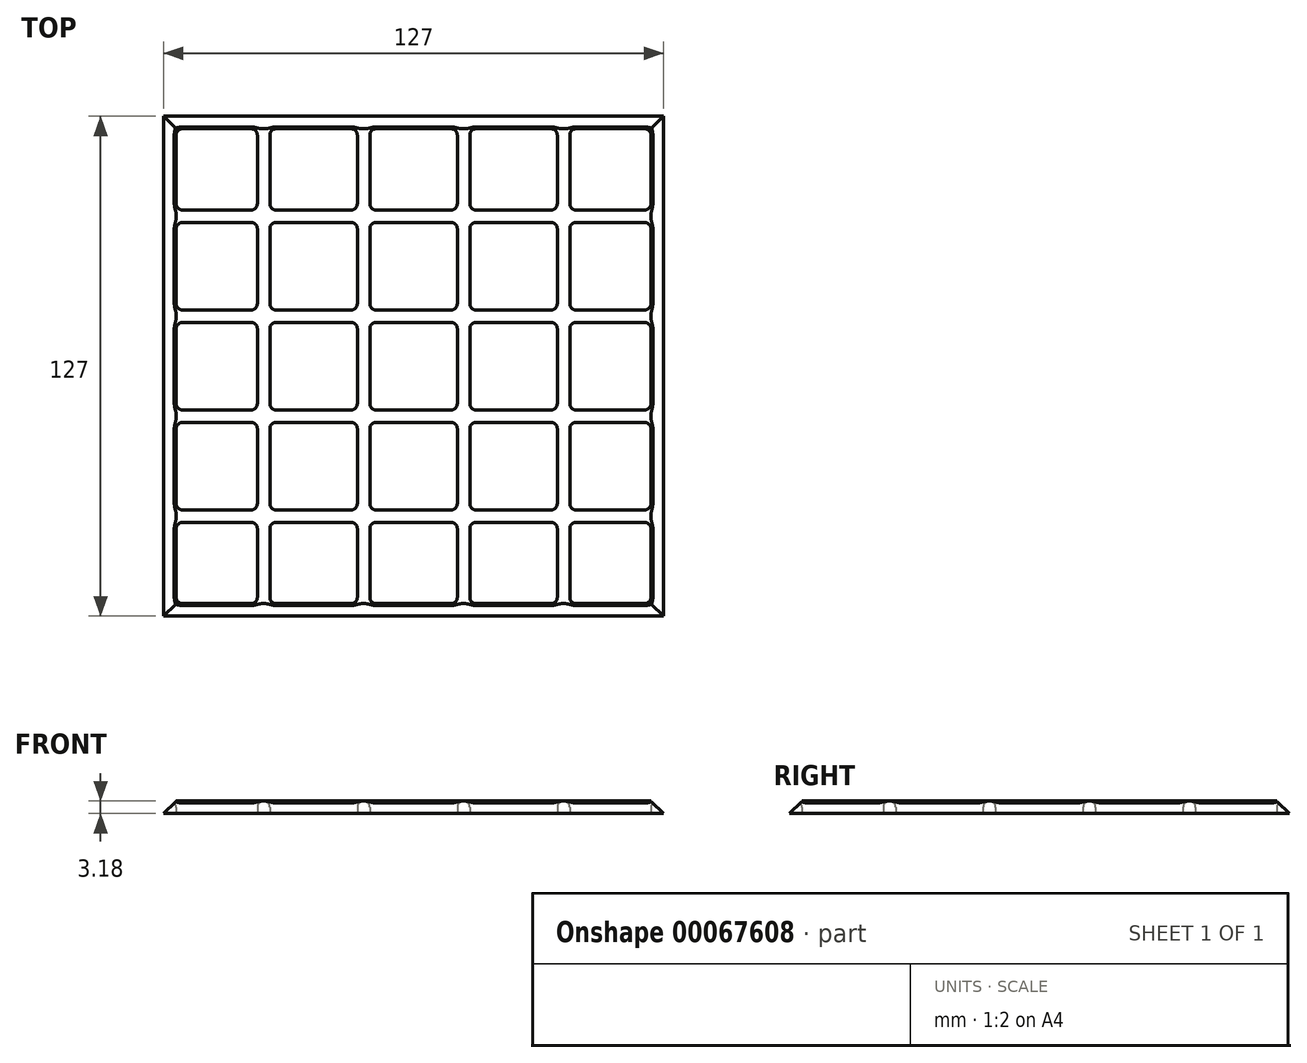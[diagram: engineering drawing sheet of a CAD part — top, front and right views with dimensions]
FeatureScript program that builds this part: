
annotation { "Feature Type Name" : "Feature", "Feature Type Description" : "" }
export const myFeature = defineFeature(function(context is Context, id is Id, definition is map)
    precondition{}
    {
        {
            var Q0;
            Q0=qCreatedBy(makeId("Top.planeOp"),FACE);
            var sketch = newSketch(context, id + "F0", { "sketchPlane" : qUnion([Q0])});
            skLineSegment(sketch, "E0.rect.bottom", {"start": v(-63.5, 63.5) * mm, "end": v(0, 63.5) * mm});
            skLineSegment(sketch, "E0.rect.left", {"start": v(-63.5, 63.5) * mm, "end": v(-63.5, 0) * mm});
            skPoint(sketch, "E0.rect.middle", {"position": v(0, 0) * mm});
            skLineSegment(sketch, "E1.bottom", {"start": v(-58.74, 60.33) * mm, "end": v(-41.27, 60.33) * mm});
            skLineSegment(sketch, "E1.top", {"start": v(-58.74, 39.69) * mm, "end": v(-41.27, 39.69) * mm});
            skLineSegment(sketch, "E1.left", {"start": v(-60.32, 58.74) * mm, "end": v(-60.32, 41.27) * mm});
            skLineSegment(sketch, "E1.right", {"start": v(-39.69, 58.74) * mm, "end": v(-39.69, 41.27) * mm});
            skLineSegment(sketch, "E2.top", {"start": v(-63.5, 38.1) * mm, "end": v(-38.1, 38.1) * mm, "construction": true});
            skLineSegment(sketch, "E2.right", {"start": v(-38.1, 63.5) * mm, "end": v(-38.1, 38.1) * mm, "construction": true});
            skPoint(sketch, "E3.visualSharp", {"position": v(-60.32, 60.33) * mm});
            skArc(sketch, "E3.filletArc", {"start": v(-58.74, 60.33) * mm, "mid": v(-59.86, 59.86) * mm, "end": v(-60.33, 58.74) * mm});
            skPoint(sketch, "E4.visualSharp", {"position": v(-60.33, 39.69) * mm});
            skArc(sketch, "E4.filletArc", {"start": v(-60.32, 41.27) * mm, "mid": v(-59.86, 40.15) * mm, "end": v(-58.74, 39.69) * mm});
            skPoint(sketch, "E5.visualSharp", {"position": v(-39.69, 39.69) * mm});
            skArc(sketch, "E5.filletArc", {"start": v(-41.27, 39.69) * mm, "mid": v(-40.15, 40.15) * mm, "end": v(-39.69, 41.27) * mm});
            skPoint(sketch, "E6.visualSharp", {"position": v(-39.69, 60.33) * mm});
            skArc(sketch, "E6.filletArc", {"start": v(-39.69, 58.74) * mm, "mid": v(-40.15, 59.86) * mm, "end": v(-41.27, 60.33) * mm});
            skPoint(sketch, "E7.oppositeSnap0", {"position": v(-50, 39.69) * mm});
            skLineSegment(sketch, "E7.bottom", {"start": v(-34.92, 60.33) * mm, "end": v(-15.87, 60.33) * mm});
            skLineSegment(sketch, "E7.top", {"start": v(-34.92, 39.69) * mm, "end": v(-15.87, 39.69) * mm});
            skLineSegment(sketch, "E7.left", {"start": v(-36.51, 58.74) * mm, "end": v(-36.51, 41.27) * mm});
            skLineSegment(sketch, "E7.right", {"start": v(-14.29, 58.74) * mm, "end": v(-14.29, 41.27) * mm});
            skLineSegment(sketch, "E8.bottom", {"start": v(-9.53, 60.33) * mm, "end": v(0, 60.33) * mm});
            skLineSegment(sketch, "E8.top", {"start": v(-9.53, 39.69) * mm, "end": v(0, 39.69) * mm});
            skLineSegment(sketch, "E8.left", {"start": v(-11.11, 58.74) * mm, "end": v(-11.11, 41.27) * mm});
            skLineSegment(sketch, "E9", {"start": v(-12.7, 63.5) * mm, "end": v(-12.7, 38.1) * mm, "construction": true});
            skPoint(sketch, "E10.visualSharp", {"position": v(-36.51, 60.33) * mm});
            skArc(sketch, "E10.filletArc", {"start": v(-34.92, 60.33) * mm, "mid": v(-36.05, 59.86) * mm, "end": v(-36.51, 58.74) * mm});
            skPoint(sketch, "E11.visualSharp", {"position": v(-36.51, 39.69) * mm});
            skArc(sketch, "E11.filletArc", {"start": v(-36.51, 41.27) * mm, "mid": v(-36.05, 40.15) * mm, "end": v(-34.92, 39.69) * mm});
            skPoint(sketch, "E12.visualSharp", {"position": v(-14.29, 39.69) * mm});
            skArc(sketch, "E12.filletArc", {"start": v(-15.87, 39.69) * mm, "mid": v(-14.75, 40.15) * mm, "end": v(-14.29, 41.27) * mm});
            skPoint(sketch, "E13.visualSharp", {"position": v(-14.29, 60.33) * mm});
            skArc(sketch, "E13.filletArc", {"start": v(-14.29, 58.74) * mm, "mid": v(-14.75, 59.86) * mm, "end": v(-15.87, 60.33) * mm});
            skPoint(sketch, "E14.visualSharp", {"position": v(-11.11, 60.33) * mm});
            skArc(sketch, "E14.filletArc", {"start": v(-9.53, 60.33) * mm, "mid": v(-10.65, 59.86) * mm, "end": v(-11.11, 58.74) * mm});
            skPoint(sketch, "E15.visualSharp", {"position": v(-11.11, 39.69) * mm});
            skArc(sketch, "E15.filletArc", {"start": v(-11.11, 41.27) * mm, "mid": v(-10.65, 40.15) * mm, "end": v(-9.53, 39.69) * mm});
            skLineSegment(sketch, "E16", {"start": v(-11.11, 0) * mm, "end": v(-14.29, 0) * mm});
            skLineSegment(sketch, "E17", {"start": v(0, 11.11) * mm, "end": v(0, 14.29) * mm});
            skLineSegment(sketch, "E18", {"start": v(0, 60.33) * mm, "end": v(0, 63.5) * mm});
            skLineSegment(sketch, "E19.bottom", {"start": v(-58.74, 36.51) * mm, "end": v(-41.27, 36.51) * mm});
            skLineSegment(sketch, "E19.top", {"start": v(-58.74, 14.29) * mm, "end": v(-41.27, 14.29) * mm});
            skLineSegment(sketch, "E19.left", {"start": v(-60.33, 34.93) * mm, "end": v(-60.33, 15.87) * mm});
            skLineSegment(sketch, "E19.right", {"start": v(-39.69, 34.93) * mm, "end": v(-39.69, 15.87) * mm});
            skLineSegment(sketch, "E20.bottom", {"start": v(-34.93, 36.51) * mm, "end": v(-15.87, 36.51) * mm});
            skLineSegment(sketch, "E20.top", {"start": v(-34.93, 14.29) * mm, "end": v(-15.87, 14.29) * mm});
            skLineSegment(sketch, "E20.left", {"start": v(-36.51, 34.93) * mm, "end": v(-36.51, 15.87) * mm});
            skLineSegment(sketch, "E20.right", {"start": v(-14.29, 34.93) * mm, "end": v(-14.29, 15.87) * mm});
            skLineSegment(sketch, "E21.bottom", {"start": v(-58.74, 11.11) * mm, "end": v(-41.27, 11.11) * mm});
            skLineSegment(sketch, "E21.left", {"start": v(-60.33, 9.52) * mm, "end": v(-60.33, 0) * mm});
            skLineSegment(sketch, "E21.right", {"start": v(-39.69, 9.52) * mm, "end": v(-39.69, 0) * mm});
            skLineSegment(sketch, "E22.bottom", {"start": v(-34.92, 11.11) * mm, "end": v(-15.87, 11.11) * mm});
            skLineSegment(sketch, "E22.left", {"start": v(-36.51, 9.52) * mm, "end": v(-36.51, 0) * mm});
            skLineSegment(sketch, "E22.right", {"start": v(-14.29, 9.53) * mm, "end": v(-14.29, 0) * mm});
            skLineSegment(sketch, "E23.bottom", {"start": v(-9.52, 11.11) * mm, "end": v(0, 11.11) * mm});
            skLineSegment(sketch, "E23.left", {"start": v(-11.11, 9.53) * mm, "end": v(-11.11, 0) * mm});
            skLineSegment(sketch, "E24.bottom", {"start": v(-9.52, 36.51) * mm, "end": v(0, 36.51) * mm});
            skLineSegment(sketch, "E24.top", {"start": v(-9.52, 14.29) * mm, "end": v(0, 14.29) * mm});
            skLineSegment(sketch, "E24.left", {"start": v(-11.11, 34.93) * mm, "end": v(-11.11, 15.87) * mm});
            skLineSegment(sketch, "E25.trimOffspring", {"start": v(-60.33, 0) * mm, "end": v(-63.5, 0) * mm});
            skLineSegment(sketch, "E26.trimOffspring", {"start": v(-36.51, 0) * mm, "end": v(-39.69, 0) * mm});
            skLineSegment(sketch, "E27.trimOffspring", {"start": v(0, 36.51) * mm, "end": v(0, 39.69) * mm});
            skLineSegment(sketch, "E28", {"start": v(-63.5, 12.7) * mm, "end": v(0, 12.7) * mm, "construction": true});
            skPoint(sketch, "E29.visualSharp", {"position": v(-60.33, 36.51) * mm});
            skArc(sketch, "E29.filletArc", {"start": v(-58.74, 36.51) * mm, "mid": v(-59.86, 36.05) * mm, "end": v(-60.33, 34.93) * mm});
            skPoint(sketch, "E30.visualSharp", {"position": v(-60.33, 14.29) * mm});
            skArc(sketch, "E30.filletArc", {"start": v(-60.33, 15.87) * mm, "mid": v(-59.86, 14.75) * mm, "end": v(-58.74, 14.29) * mm});
            skPoint(sketch, "E31.visualSharp", {"position": v(-39.69, 36.51) * mm});
            skArc(sketch, "E31.filletArc", {"start": v(-39.69, 34.93) * mm, "mid": v(-40.15, 36.05) * mm, "end": v(-41.27, 36.51) * mm});
            skPoint(sketch, "E32.visualSharp", {"position": v(-39.69, 14.29) * mm});
            skArc(sketch, "E32.filletArc", {"start": v(-41.27, 14.29) * mm, "mid": v(-40.15, 14.75) * mm, "end": v(-39.69, 15.87) * mm});
            skPoint(sketch, "E33.visualSharp", {"position": v(-36.51, 14.29) * mm});
            skArc(sketch, "E33.filletArc", {"start": v(-36.51, 15.87) * mm, "mid": v(-36.05, 14.75) * mm, "end": v(-34.93, 14.29) * mm});
            skPoint(sketch, "E34.visualSharp", {"position": v(-36.51, 36.51) * mm});
            skArc(sketch, "E34.filletArc", {"start": v(-34.93, 36.51) * mm, "mid": v(-36.05, 36.05) * mm, "end": v(-36.51, 34.93) * mm});
            skPoint(sketch, "E35.visualSharp", {"position": v(-14.29, 36.51) * mm});
            skArc(sketch, "E35.filletArc", {"start": v(-14.29, 34.93) * mm, "mid": v(-14.75, 36.05) * mm, "end": v(-15.87, 36.51) * mm});
            skPoint(sketch, "E36.visualSharp", {"position": v(-14.29, 14.29) * mm});
            skArc(sketch, "E36.filletArc", {"start": v(-15.87, 14.29) * mm, "mid": v(-14.75, 14.75) * mm, "end": v(-14.29, 15.87) * mm});
            skPoint(sketch, "E37.visualSharp", {"position": v(-11.11, 14.29) * mm});
            skArc(sketch, "E37.filletArc", {"start": v(-11.11, 15.87) * mm, "mid": v(-10.65, 14.75) * mm, "end": v(-9.52, 14.29) * mm});
            skPoint(sketch, "E38.visualSharp", {"position": v(-11.11, 36.51) * mm});
            skArc(sketch, "E38.filletArc", {"start": v(-9.52, 36.51) * mm, "mid": v(-10.65, 36.05) * mm, "end": v(-11.11, 34.93) * mm});
            skPoint(sketch, "E39.visualSharp", {"position": v(-11.11, 11.11) * mm});
            skArc(sketch, "E39.filletArc", {"start": v(-9.52, 11.11) * mm, "mid": v(-10.65, 10.65) * mm, "end": v(-11.11, 9.53) * mm});
            skPoint(sketch, "E40.visualSharp", {"position": v(-14.29, 11.11) * mm});
            skArc(sketch, "E40.filletArc", {"start": v(-14.29, 9.53) * mm, "mid": v(-14.75, 10.65) * mm, "end": v(-15.87, 11.11) * mm});
            skPoint(sketch, "E41.visualSharp", {"position": v(-36.51, 11.11) * mm});
            skArc(sketch, "E41.filletArc", {"start": v(-34.92, 11.11) * mm, "mid": v(-36.05, 10.65) * mm, "end": v(-36.51, 9.52) * mm});
            skPoint(sketch, "E42.visualSharp", {"position": v(-60.33, 11.11) * mm});
            skArc(sketch, "E42.filletArc", {"start": v(-58.74, 11.11) * mm, "mid": v(-59.86, 10.65) * mm, "end": v(-60.33, 9.52) * mm});
            skPoint(sketch, "E43.visualSharp", {"position": v(-39.69, 11.11) * mm});
            skArc(sketch, "E43.filletArc", {"start": v(-39.69, 9.52) * mm, "mid": v(-40.15, 10.65) * mm, "end": v(-41.27, 11.11) * mm});
            skSolve(sketch);
        }
        {
            var Q0;
            Q0 = qSketchRegion(id + "F0", true);
            extrude(context, id + "F1", {"entities" : qUnion([Q0]), "depth" : 3.17 * mm});
        }
        {
            var Q0;
            Q0=makeQuery(id+"F1.opExtrude","CAP_EDGE",EDGE,{"disambiguationData":[OSD([sQuery(id+"F0.wireOp",EDGE,"E1.left")])],"isStart":false});
            var Q1;
            Q1=makeQuery(id+"F1.opExtrude","CAP_EDGE",EDGE,{"disambiguationData":[OSD([sQuery(id+"F0.wireOp",EDGE,"E19.left")])],"isStart":false});
            var Q2;
            Q2=makeQuery(id+"F1.opExtrude","CAP_EDGE",EDGE,{"disambiguationData":[OSD([sQuery(id+"F0.wireOp",EDGE,"E20.left")])],"isStart":false});
            var Q3;
            Q3=makeQuery(id+"F1.opExtrude","CAP_EDGE",EDGE,{"disambiguationData":[OSD([sQuery(id+"F0.wireOp",EDGE,"E7.left")])],"isStart":false});
            var Q4;
            Q4=makeQuery(id+"F1.opExtrude","CAP_EDGE",EDGE,{"disambiguationData":[OSD([sQuery(id+"F0.wireOp",EDGE,"E8.left")])],"isStart":false});
            var Q5;
            Q5=makeQuery(id+"F1.opExtrude","CAP_EDGE",EDGE,{"disambiguationData":[OSD([sQuery(id+"F0.wireOp",EDGE,"E24.left")])],"isStart":false});
            var Q6;
            Q6=makeQuery(id+"F1.opExtrude","CAP_EDGE",EDGE,{"disambiguationData":[OSD([sQuery(id+"F0.wireOp",EDGE,"E22.bottom")])],"isStart":false});
            var Q7;
            Q7=makeQuery(id+"F1.opExtrude","CAP_EDGE",EDGE,{"disambiguationData":[OSD([sQuery(id+"F0.wireOp",EDGE,"E21.bottom")])],"isStart":false});
            var Q8;
            Q8=makeQuery(id+"F1.opExtrude","CAP_EDGE",EDGE,{"disambiguationData":[OSD([sQuery(id+"F0.wireOp",EDGE,"E23.bottom")])],"isStart":false});
            fillet(context, id + "F2", {"entities" : qUnion([Q0, Q1, Q2, Q3, Q4, Q5, Q6, Q7, Q8]), "radius" : 1.59 * mm, "tangentPropagation" : true, "allowEdgeOverflow" : false});
        }
        {
            var Q0;
            Q0=makeQuery(id+"F1.opExtrude","SWEPT_BODY",BODY,{"disambiguationData":[OSD([sQuery(id+"F0.wireOp",EDGE,"E0.rect.bottom"),sQuery(id+"F0.wireOp",EDGE,"E0.rect.left"),sQuery(id+"F0.wireOp",EDGE,"E1.bottom"),sQuery(id+"F0.wireOp",EDGE,"E1.top"),sQuery(id+"F0.wireOp",EDGE,"E1.left"),sQuery(id+"F0.wireOp",EDGE,"E1.right"),sQuery(id+"F0.wireOp",EDGE,"E3.filletArc"),sQuery(id+"F0.wireOp",EDGE,"E4.filletArc"),sQuery(id+"F0.wireOp",EDGE,"E5.filletArc"),sQuery(id+"F0.wireOp",EDGE,"E6.filletArc"),sQuery(id+"F0.wireOp",EDGE,"28f6a927-1c7f-40b6-a826-a70ca0bd145b.filletArc"),sQuery(id+"F0.wireOp",EDGE,"E7.bottom"),sQuery(id+"F0.wireOp",EDGE,"E7.top"),sQuery(id+"F0.wireOp",EDGE,"E7.left"),sQuery(id+"F0.wireOp",EDGE,"E7.right"),sQuery(id+"F0.wireOp",EDGE,"E8.bottom"),sQuery(id+"F0.wireOp",EDGE,"E8.top"),sQuery(id+"F0.wireOp",EDGE,"E8.left"),sQuery(id+"F0.wireOp",EDGE,"E10.filletArc"),sQuery(id+"F0.wireOp",EDGE,"E11.filletArc"),sQuery(id+"F0.wireOp",EDGE,"E12.filletArc"),sQuery(id+"F0.wireOp",EDGE,"E13.filletArc"),sQuery(id+"F0.wireOp",EDGE,"E14.filletArc"),sQuery(id+"F0.wireOp",EDGE,"E15.filletArc"),sQuery(id+"F0.wireOp",EDGE,"E16"),sQuery(id+"F0.wireOp",EDGE,"E17"),sQuery(id+"F0.wireOp",EDGE,"E18"),sQuery(id+"F0.wireOp",EDGE,"E19.bottom"),sQuery(id+"F0.wireOp",EDGE,"E19.top"),sQuery(id+"F0.wireOp",EDGE,"E19.left"),sQuery(id+"F0.wireOp",EDGE,"E19.right"),sQuery(id+"F0.wireOp",EDGE,"E20.bottom"),sQuery(id+"F0.wireOp",EDGE,"E20.top"),sQuery(id+"F0.wireOp",EDGE,"E20.left"),sQuery(id+"F0.wireOp",EDGE,"E20.right"),sQuery(id+"F0.wireOp",EDGE,"E21.bottom"),sQuery(id+"F0.wireOp",EDGE,"E21.left"),sQuery(id+"F0.wireOp",EDGE,"E21.right"),sQuery(id+"F0.wireOp",EDGE,"E22.bottom"),sQuery(id+"F0.wireOp",EDGE,"E22.left"),sQuery(id+"F0.wireOp",EDGE,"E22.right"),sQuery(id+"F0.wireOp",EDGE,"E23.bottom"),sQuery(id+"F0.wireOp",EDGE,"E23.left"),sQuery(id+"F0.wireOp",EDGE,"E24.bottom"),sQuery(id+"F0.wireOp",EDGE,"E24.top"),sQuery(id+"F0.wireOp",EDGE,"E24.left"),sQuery(id+"F0.wireOp",EDGE,"E25.trimOffspring"),sQuery(id+"F0.wireOp",EDGE,"E26.trimOffspring"),sQuery(id+"F0.wireOp",EDGE,"E27.trimOffspring")])]});
            var Q1;
            Q1=qCreatedBy(makeId("Right.planeOp"),FACE);
            mirror(context, id + "F3", {"operationType" : NewBodyOperationType.ADD, "entities" : qUnion([Q0]), "mirrorPlane" : qUnion([Q1])});
        }
        {
            var Q0;
            Q0=makeQuery(id+"F1.opExtrude","SWEPT_BODY",BODY,{"disambiguationData":[OSD([sQuery(id+"F0.wireOp",EDGE,"E0.rect.bottom"),sQuery(id+"F0.wireOp",EDGE,"E0.rect.left"),sQuery(id+"F0.wireOp",EDGE,"E1.bottom"),sQuery(id+"F0.wireOp",EDGE,"E1.top"),sQuery(id+"F0.wireOp",EDGE,"E1.left"),sQuery(id+"F0.wireOp",EDGE,"E1.right"),sQuery(id+"F0.wireOp",EDGE,"E3.filletArc"),sQuery(id+"F0.wireOp",EDGE,"E4.filletArc"),sQuery(id+"F0.wireOp",EDGE,"E5.filletArc"),sQuery(id+"F0.wireOp",EDGE,"E6.filletArc"),sQuery(id+"F0.wireOp",EDGE,"28f6a927-1c7f-40b6-a826-a70ca0bd145b.filletArc"),sQuery(id+"F0.wireOp",EDGE,"E7.bottom"),sQuery(id+"F0.wireOp",EDGE,"E7.top"),sQuery(id+"F0.wireOp",EDGE,"E7.left"),sQuery(id+"F0.wireOp",EDGE,"E7.right"),sQuery(id+"F0.wireOp",EDGE,"E8.bottom"),sQuery(id+"F0.wireOp",EDGE,"E8.top"),sQuery(id+"F0.wireOp",EDGE,"E8.left"),sQuery(id+"F0.wireOp",EDGE,"E10.filletArc"),sQuery(id+"F0.wireOp",EDGE,"E11.filletArc"),sQuery(id+"F0.wireOp",EDGE,"E12.filletArc"),sQuery(id+"F0.wireOp",EDGE,"E13.filletArc"),sQuery(id+"F0.wireOp",EDGE,"E14.filletArc"),sQuery(id+"F0.wireOp",EDGE,"E15.filletArc"),sQuery(id+"F0.wireOp",EDGE,"E16"),sQuery(id+"F0.wireOp",EDGE,"E17"),sQuery(id+"F0.wireOp",EDGE,"E18"),sQuery(id+"F0.wireOp",EDGE,"E19.bottom"),sQuery(id+"F0.wireOp",EDGE,"E19.top"),sQuery(id+"F0.wireOp",EDGE,"E19.left"),sQuery(id+"F0.wireOp",EDGE,"E19.right"),sQuery(id+"F0.wireOp",EDGE,"E20.bottom"),sQuery(id+"F0.wireOp",EDGE,"E20.top"),sQuery(id+"F0.wireOp",EDGE,"E20.left"),sQuery(id+"F0.wireOp",EDGE,"E20.right"),sQuery(id+"F0.wireOp",EDGE,"E21.bottom"),sQuery(id+"F0.wireOp",EDGE,"E21.left"),sQuery(id+"F0.wireOp",EDGE,"E21.right"),sQuery(id+"F0.wireOp",EDGE,"E22.bottom"),sQuery(id+"F0.wireOp",EDGE,"E22.left"),sQuery(id+"F0.wireOp",EDGE,"E22.right"),sQuery(id+"F0.wireOp",EDGE,"E23.bottom"),sQuery(id+"F0.wireOp",EDGE,"E23.left"),sQuery(id+"F0.wireOp",EDGE,"E24.bottom"),sQuery(id+"F0.wireOp",EDGE,"E24.top"),sQuery(id+"F0.wireOp",EDGE,"E24.left"),sQuery(id+"F0.wireOp",EDGE,"E25.trimOffspring"),sQuery(id+"F0.wireOp",EDGE,"E26.trimOffspring"),sQuery(id+"F0.wireOp",EDGE,"E27.trimOffspring")])]});
            var Q1;
            Q1=qCreatedBy(makeId("Front.planeOp"),FACE);
            mirror(context, id + "F4", {"operationType" : NewBodyOperationType.ADD, "entities" : qUnion([Q0]), "mirrorPlane" : qUnion([Q1])});
        }
        {
            var Q0;
            {var subQ0=makeQuery(id+"F1.opExtrude","CAP_EDGE",EDGE,{"disambiguationData":[OSD([sQuery(id+"F0.wireOp",EDGE,"E0.rect.bottom")])],"isStart":false});Q0=makeQuery(id+"F3.boolean.opBoolean","MERGE",EDGE,{"derivedFrom":[subQ0,makeQuery(id+"F3.opPattern","COPY",EDGE,{"derivedFrom":subQ0,"instanceName":"1"})]});}
            var Q1;
            {var subQ0=makeQuery(id+"F1.opExtrude","CAP_EDGE",EDGE,{"disambiguationData":[OSD([sQuery(id+"F0.wireOp",EDGE,"E0.rect.left")])],"isStart":false});Q1=makeQuery(id+"F4.boolean.opBoolean","MERGE",EDGE,{"derivedFrom":[subQ0,makeQuery(id+"F4.opPattern","COPY",EDGE,{"derivedFrom":subQ0,"instanceName":"1"})]});}
            var Q2;
            {var subQ0=makeQuery(id+"F1.opExtrude","CAP_EDGE",EDGE,{"disambiguationData":[OSD([sQuery(id+"F0.wireOp",EDGE,"E0.rect.bottom")])],"isStart":false});Q2=makeQuery(id+"F4.opPattern","COPY",EDGE,{"derivedFrom":makeQuery(id+"F3.boolean.opBoolean","MERGE",EDGE,{"derivedFrom":[subQ0,makeQuery(id+"F3.opPattern","COPY",EDGE,{"derivedFrom":subQ0,"instanceName":"1"})]}),"instanceName":"1"});}
            var Q3;
            {var subQ0=makeQuery(id+"F3.opPattern","COPY",EDGE,{"derivedFrom":makeQuery(id+"F1.opExtrude","CAP_EDGE",EDGE,{"disambiguationData":[OSD([sQuery(id+"F0.wireOp",EDGE,"E0.rect.left")])],"isStart":false}),"instanceName":"1"});Q3=makeQuery(id+"F4.boolean.opBoolean","MERGE",EDGE,{"derivedFrom":[subQ0,makeQuery(id+"F4.opPattern","COPY",EDGE,{"derivedFrom":subQ0,"instanceName":"1"})]});}
            chamfer(context, id + "F5", {"entities" : qUnion([Q0, Q1, Q2, Q3]), "width" : 3.17 * mm, "tangentPropagation" : true});
        }
    });
